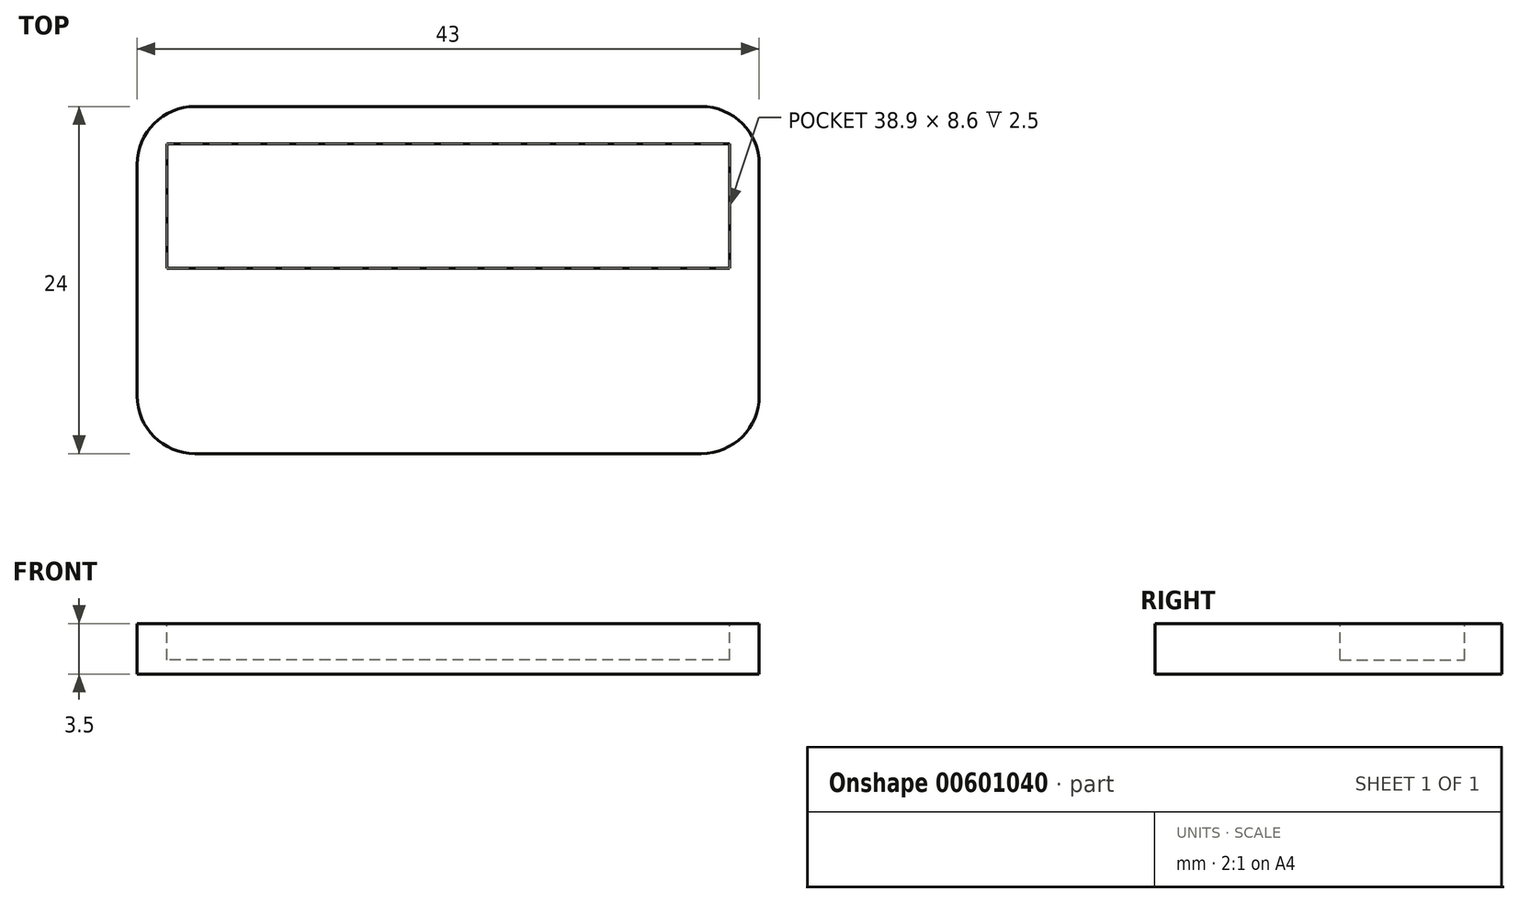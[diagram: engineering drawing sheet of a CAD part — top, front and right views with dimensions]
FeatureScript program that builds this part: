
annotation { "Feature Type Name" : "Feature", "Feature Type Description" : "" }
export const myFeature = defineFeature(function(context is Context, id is Id, definition is map)
    precondition{}
    {
        {
            var Q0;
            Q0=qCreatedBy(makeId("Top.planeOp"),FACE);
            var sketch = newSketch(context, id + "F0", { "sketchPlane" : qUnion([Q0])});
            skLineSegment(sketch, "E0.bottom", {"start": v(17.5, -12) * mm, "end": v(-17.5, -12) * mm});
            skLineSegment(sketch, "E0.top", {"start": v(17.5, 12) * mm, "end": v(-17.5, 12) * mm});
            skLineSegment(sketch, "E0.left", {"start": v(21.5, -8) * mm, "end": v(21.5, 8) * mm});
            skLineSegment(sketch, "E0.right", {"start": v(-21.5, -8) * mm, "end": v(-21.5, 8) * mm});
            skPoint(sketch, "E0.middle", {"position": v(0, 0) * mm});
            skPoint(sketch, "E1.visualSharp", {"position": v(-21.5, 12) * mm});
            skArc(sketch, "E1.filletArc", {"start": v(-17.5, 12) * mm, "mid": v(-20.33, 10.83) * mm, "end": v(-21.5, 8) * mm});
            skPoint(sketch, "E2.visualSharp", {"position": v(21.5, 12) * mm});
            skArc(sketch, "E2.filletArc", {"start": v(21.5, 8) * mm, "mid": v(20.33, 10.83) * mm, "end": v(17.5, 12) * mm});
            skPoint(sketch, "E3.visualSharp", {"position": v(21.5, -12) * mm});
            skArc(sketch, "E3.filletArc", {"start": v(17.5, -12) * mm, "mid": v(20.33, -10.83) * mm, "end": v(21.5, -8) * mm});
            skPoint(sketch, "E4.visualSharp", {"position": v(-21.5, -12) * mm});
            skArc(sketch, "E4.filletArc", {"start": v(-21.5, -8) * mm, "mid": v(-20.33, -10.83) * mm, "end": v(-17.5, -12) * mm});
            skSolve(sketch);
        }
        {
            var Q0;
            Q0=makeQuery(id+"F0.imprint","IMPRINT",FACE,{"disambiguationData":[TD([[makeQuery(id+"F0.imprint","IMPRINT",EDGE,{"derivedFrom":sQuery(id+"F0.wireOp",EDGE,"E0.bottom")}),-1.0]])]});
            extrude(context, id + "F1", {"entities" : qUnion([Q0]), "depth" : 3.5 * mm, "offsetDistance" : 25 * mm});
        }
        {
            var Q0;
            Q0=makeQuery(id+"F1.opExtrude","CAP_FACE",FACE,{"disambiguationData":[OSD([sQuery(id+"F0.wireOp",EDGE,"E0.bottom"),sQuery(id+"F0.wireOp",EDGE,"E0.top"),sQuery(id+"F0.wireOp",EDGE,"E0.left"),sQuery(id+"F0.wireOp",EDGE,"E0.right"),sQuery(id+"F0.wireOp",EDGE,"E1.filletArc"),sQuery(id+"F0.wireOp",EDGE,"E2.filletArc"),sQuery(id+"F0.wireOp",EDGE,"E3.filletArc"),sQuery(id+"F0.wireOp",EDGE,"E4.filletArc")])],"isStart":false});
            var sketch = newSketch(context, id + "F2", { "sketchPlane" : qUnion([Q0])});
            skLineSegment(sketch, "E5", {"start": v(0, 0) * mm, "end": v(0, 12) * mm, "construction": true});
            skLineSegment(sketch, "E6.bottom", {"start": v(19.45, 0.81) * mm, "end": v(-19.45, 0.81) * mm});
            skLineSegment(sketch, "E6.top", {"start": v(19.45, 9.41) * mm, "end": v(-19.45, 9.41) * mm});
            skLineSegment(sketch, "E6.left", {"start": v(19.45, 0.81) * mm, "end": v(19.45, 9.41) * mm});
            skLineSegment(sketch, "E6.right", {"start": v(-19.45, 0.81) * mm, "end": v(-19.45, 9.41) * mm});
            skPoint(sketch, "E6.middle", {"position": v(0, 5.11) * mm});
            skSolve(sketch);
        }
        {
            var Q0;
            Q0=makeQuery(id+"F2.imprint","IMPRINT",FACE,{"disambiguationData":[TD([[makeQuery(id+"F2.imprint","IMPRINT",EDGE,{"derivedFrom":sQuery(id+"F2.wireOp",EDGE,"E6.bottom")}),-1.0]])]});
            extrude(context, id + "F3", {"entities" : qUnion([Q0]), "operationType" : NewBodyOperationType.REMOVE, "oppositeDirection" : true, "depth" : 2.5 * mm, "offsetDistance" : 25 * mm});
        }
    });
